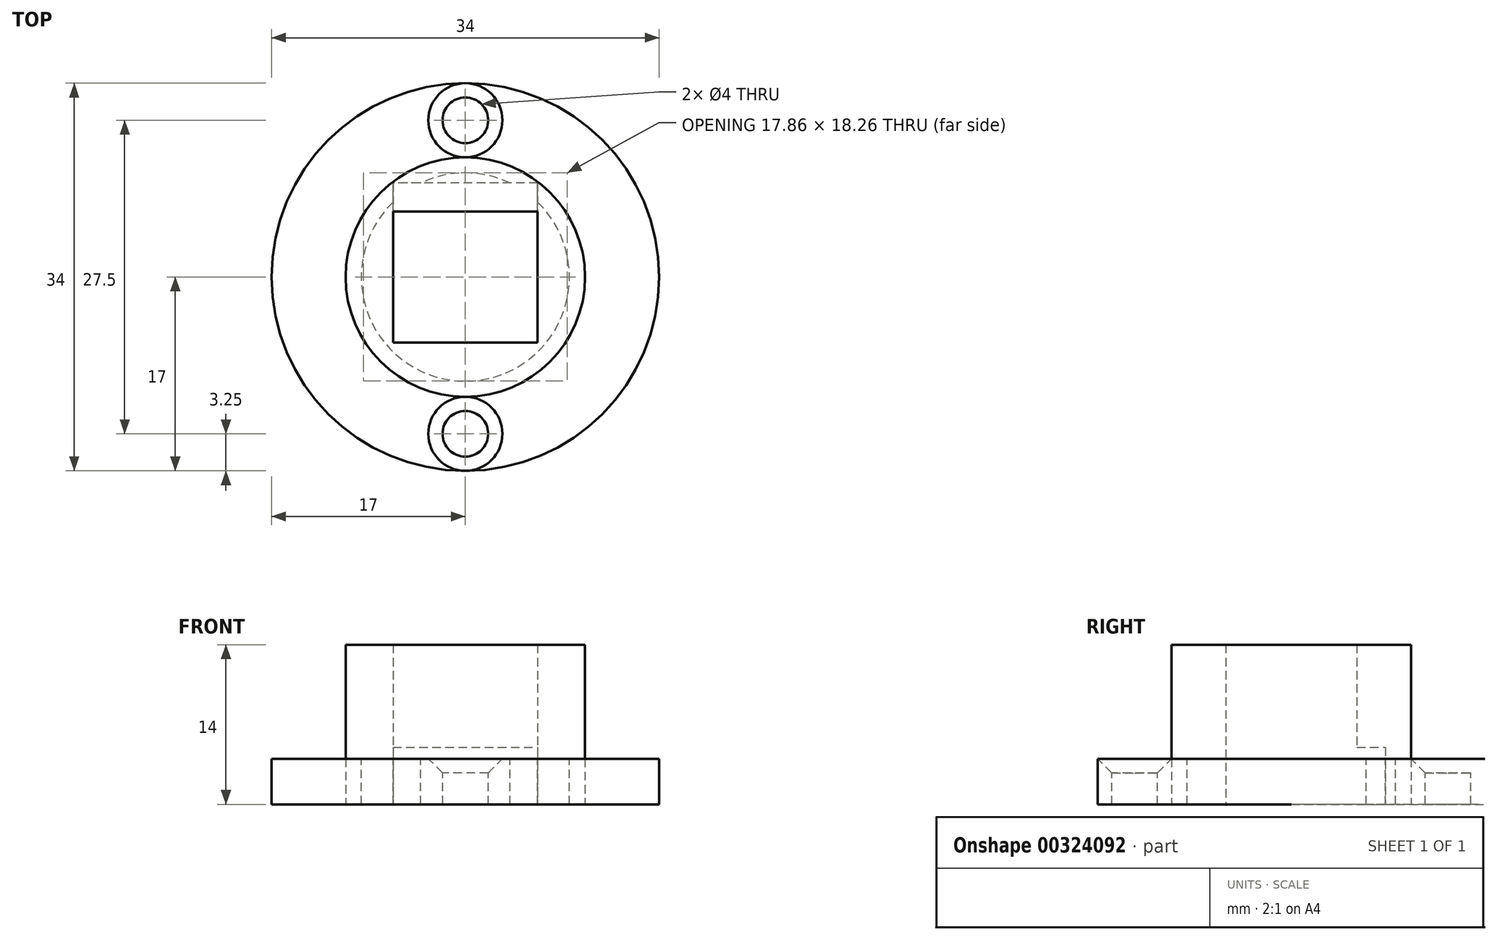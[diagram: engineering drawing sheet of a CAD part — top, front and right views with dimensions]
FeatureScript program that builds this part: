
annotation { "Feature Type Name" : "Feature", "Feature Type Description" : "" }
export const myFeature = defineFeature(function(context is Context, id is Id, definition is map)
    precondition{}
    {
        {
            var Q0;
            Q0=qCreatedBy(makeId("Top.planeOp"),FACE);
            var sketch = newSketch(context, id + "F0", { "sketchPlane" : qUnion([Q0])});
            skCircle(sketch, "E0", {"center": v(0, 0) * mm, "radius": 10.5 * mm});
            skLineSegment(sketch, "E1.bottom", {"start": v(-6.35, 5.75) * mm, "end": v(6.35, 5.75) * mm});
            skLineSegment(sketch, "E1.top", {"start": v(-6.35, -5.75) * mm, "end": v(6.35, -5.75) * mm});
            skLineSegment(sketch, "E1.left", {"start": v(-6.35, 5.75) * mm, "end": v(-6.35, -5.75) * mm});
            skLineSegment(sketch, "E1.right", {"start": v(6.35, 5.75) * mm, "end": v(6.35, -5.75) * mm});
            skSolve(sketch);
        }
        {
            var Q0;
            Q0=makeQuery(id+"F0.imprint","IMPRINT",FACE,{"disambiguationData":[TD([[makeQuery(id+"F0.imprint","IMPRINT",EDGE,{"derivedFrom":sQuery(id+"F0.wireOp",EDGE,"E0")}),1.0]])]});
            extrude(context, id + "F1", {"entities" : qUnion([Q0]), "depth" : 14 * mm});
        }
        {
            var Q0;
            Q0=makeQuery(id+"F1.opExtrude","CAP_FACE",FACE,{"disambiguationData":[OSD([sQuery(id+"F0.wireOp",EDGE,"E0"),sQuery(id+"F0.wireOp",EDGE,"E1.bottom"),sQuery(id+"F0.wireOp",EDGE,"E1.top"),sQuery(id+"F0.wireOp",EDGE,"E1.left"),sQuery(id+"F0.wireOp",EDGE,"E1.right")])],"isStart":true});
            var sketch = newSketch(context, id + "F2", { "sketchPlane" : qUnion([Q0])});
            skLineSegment(sketch, "E2.bottom", {"start": v(6.35, -3.25) * mm, "end": v(-6.35, -3.25) * mm});
            skLineSegment(sketch, "E2.top", {"start": v(6.35, -8.25) * mm, "end": v(-6.35, -8.25) * mm});
            skLineSegment(sketch, "E2.left", {"start": v(6.35, -3.25) * mm, "end": v(6.35, -8.25) * mm});
            skLineSegment(sketch, "E2.right", {"start": v(-6.35, -3.25) * mm, "end": v(-6.35, -8.25) * mm});
            skPoint(sketch, "E2.middle", {"position": v(0, -5.75) * mm});
            skSolve(sketch);
        }
        {
            var Q0;
            Q0=makeQuery(id+"F1.opExtrude","CAP_FACE",FACE,{"disambiguationData":[OSD([sQuery(id+"F0.wireOp",EDGE,"E0"),sQuery(id+"F0.wireOp",EDGE,"E1.bottom"),sQuery(id+"F0.wireOp",EDGE,"E1.top"),sQuery(id+"F0.wireOp",EDGE,"E1.left"),sQuery(id+"F0.wireOp",EDGE,"E1.right")])],"isStart":false});
            cPlane(context, id + "F3", {"entities" : qUnion([Q0]), "cplaneType" : CPlaneType.OFFSET, "offset" : 10 * mm, "oppositeDirection" : true, "width" : 150 * mm, "height" : 150 * mm});
        }
        {
            var Q0;
            Q0=qCreatedBy(id+"F3.planeOp",FACE);
            var sketch = newSketch(context, id + "F4", { "sketchPlane" : qUnion([Q0])});
            skCircle(sketch, "E3", {"center": v(0, 0) * mm, "radius": 17 * mm});
            skCircle(sketch, "E4", {"center": v(0, 0) * mm, "radius": 13.75 * mm, "construction": true});
            skCircle(sketch, "E5", {"center": v(0, 0) * mm, "radius": 9.13 * mm});
            skCircle(sketch, "E6", {"center": v(0, 13.75) * mm, "radius": 2 * mm});
            skCircle(sketch, "E7", {"center": v(0, -13.75) * mm, "radius": 2 * mm});
            skSolve(sketch);
        }
        {
            var Q0;
            Q0 = qSketchRegion(id + "F4", true);
            extrude(context, id + "F5", {"entities" : qUnion([Q0]), "oppositeDirection" : true, "depth" : 4 * mm, "offsetDistance" : 25 * mm});
        }
        {
            var Q0;
            {var subQ1=makeQuery(id+"F1.opExtrude","CAP_EDGE",EDGE,{"disambiguationData":[OSD([sQuery(id+"F0.wireOp",EDGE,"E1.bottom")])],"isStart":true});Q0=makeQuery(id+"F2.imprint","IMPRINT",FACE,{"disambiguationData":[TD([[makeQuery(id+"F2.imprint","IMPRINT",EDGE,{"derivedFrom":subQ1}),-1.0]])]});}
            extrude(context, id + "F6", {"entities" : qUnion([Q0]), "operationType" : NewBodyOperationType.REMOVE, "oppositeDirection" : true, "depth" : 5 * mm, "offsetDistance" : 25 * mm});
        }
        {
            var Q0;
            Q0=sQuery(id+"F4.wireOp",VERTEX,"E6.center");
            var Q1;
            Q1=sQuery(id+"F4.wireOp",VERTEX,"E7.center");
            var Q2;
            Q2=makeQuery(id+"F5.opExtrude","SWEPT_BODY",BODY,{"disambiguationData":[OSD([sQuery(id+"F4.wireOp",EDGE,"E3"),sQuery(id+"F4.wireOp",EDGE,"E5"),sQuery(id+"F4.wireOp",EDGE,"E6"),sQuery(id+"F4.wireOp",EDGE,"E7")])]});
            hole(context, id + "F7", {"style" : HoleStyle.C_SINK, "endStyle" : HoleEndStyle.BLIND, "holeDiameter" : 4 * mm, "cSinkDiameter" : 6.5 * mm, "cSinkAngle" : 90 * degree, "holeDepth" : 10 * mm, "tappedDepth" : 12 * mm, "tapClearance" : 3, "locations" : qUnion([Q0, Q1]), "scope" : qUnion([Q2])});
        }
    });
